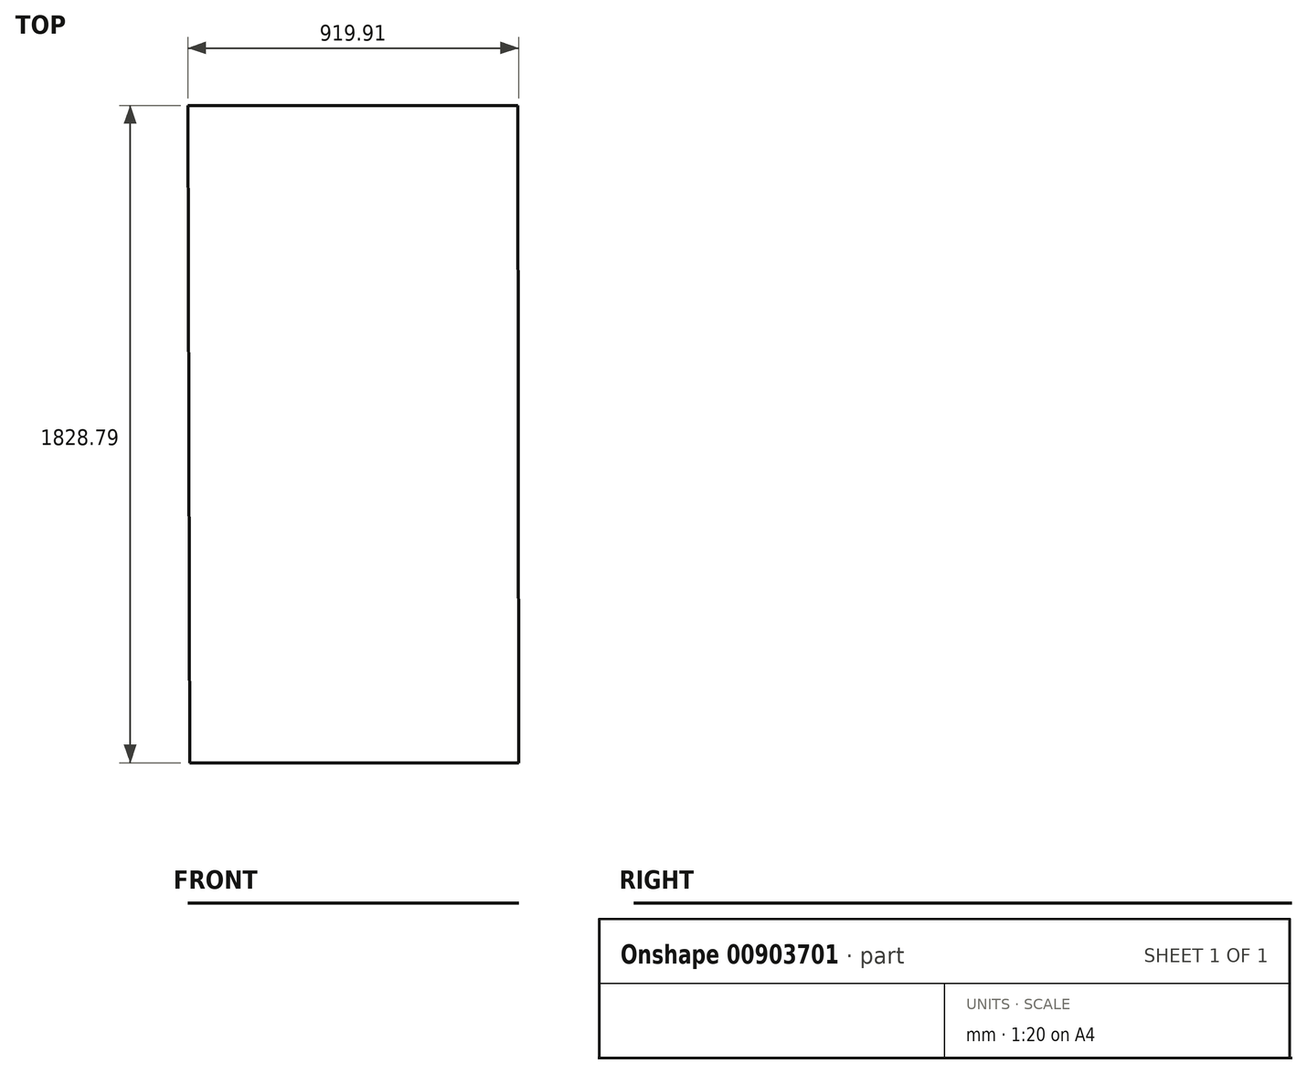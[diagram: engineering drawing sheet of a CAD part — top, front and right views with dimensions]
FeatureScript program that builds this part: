
annotation { "Feature Type Name" : "Feature", "Feature Type Description" : "" }
export const myFeature = defineFeature(function(context is Context, id is Id, definition is map)
    precondition{}
    {
        {
            var Q0;
            Q0=qCreatedBy(makeId("Top.planeOp"),FACE);
            var sketch = newSketch(context, id + "F0", { "sketchPlane" : qUnion([Q0])});
            skLineSegment(sketch, "E0", {"start": v(-36.36, -1767.9) * mm, "end": v(878.04, -1767.9) * mm});
            skLineSegment(sketch, "E1", {"start": v(878.04, -1767.9) * mm, "end": v(875.7, 60.9) * mm});
            skLineSegment(sketch, "E2", {"start": v(875.7, 60.9) * mm, "end": v(-41.87, 60.9) * mm});
            skLineSegment(sketch, "E3", {"start": v(-41.87, 60.9) * mm, "end": v(-36.36, -1767.9) * mm});
            skSolve(sketch);
        }
        {
            var Q0;
            Q0=makeQuery(id+"F0.imprint","IMPRINT",FACE,{"disambiguationData":[TD([[makeQuery(id+"F0.imprint","IMPRINT",EDGE,{"derivedFrom":sQuery(id+"F0.wireOp",EDGE,"E0")}),1.0]])]});
            extrude(context, id + "F1", {"entities" : qUnion([Q0]), "depth" : 1 / 203.2 * mm, "offsetDistance" : 25 * mm});
        }
    });
